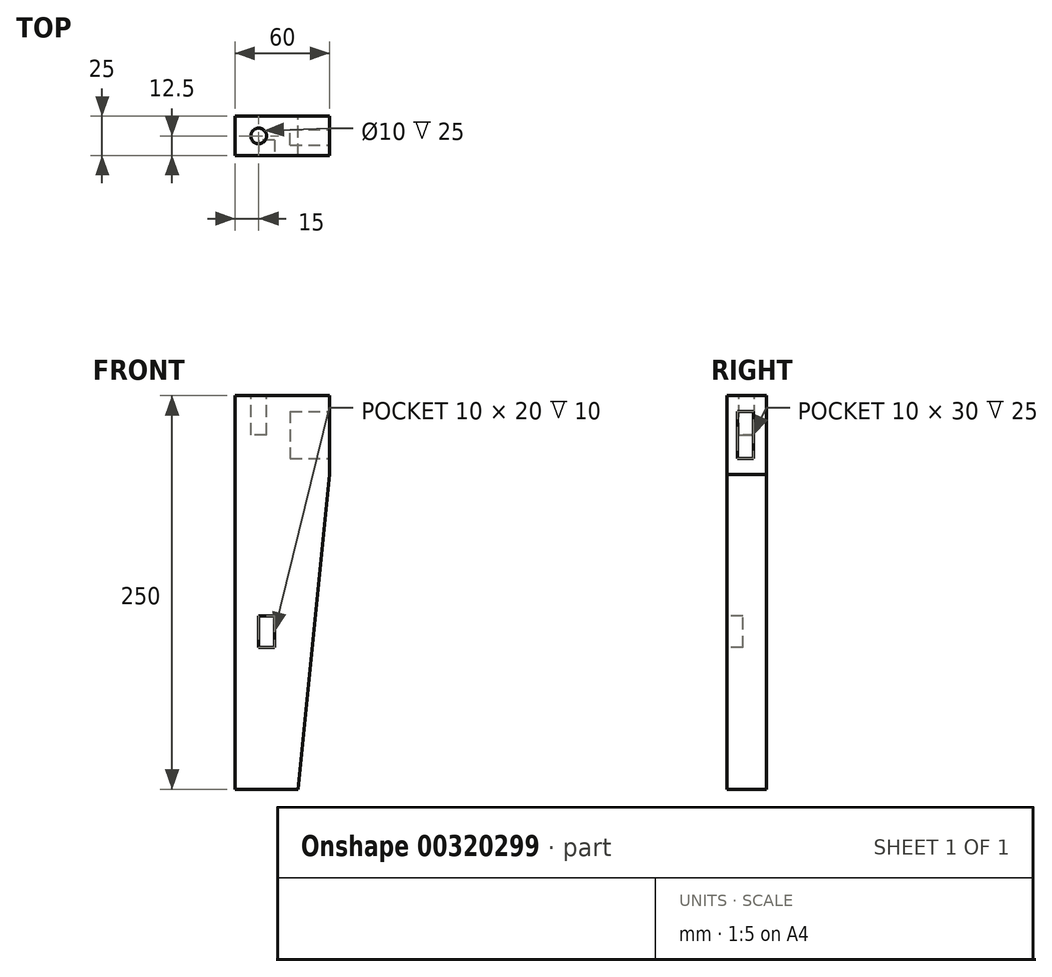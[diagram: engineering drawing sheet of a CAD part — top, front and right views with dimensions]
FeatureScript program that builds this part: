
annotation { "Feature Type Name" : "Feature", "Feature Type Description" : "" }
export const myFeature = defineFeature(function(context is Context, id is Id, definition is map)
    precondition{}
    {
        {
            var Q0;
            Q0=qCreatedBy(makeId("Front.planeOp"),FACE);
            var sketch = newSketch(context, id + "F0", { "sketchPlane" : qUnion([Q0])});
            skLineSegment(sketch, "E0.bottom", {"start": v(-30, 186.93) * mm, "end": v(30, 186.93) * mm});
            skLineSegment(sketch, "E0.left", {"start": v(-30, 186.93) * mm, "end": v(-30, -63.07) * mm});
            skPoint(sketch, "E0.middle", {"position": v(0, 61.93) * mm});
            skLineSegment(sketch, "E1", {"start": v(30, 186.93) * mm, "end": v(30, 136.93) * mm});
            skLineSegment(sketch, "E2", {"start": v(-30, -63.07) * mm, "end": v(10, -63.07) * mm});
            skLineSegment(sketch, "E3", {"start": v(30, 136.93) * mm, "end": v(10, -63.07) * mm});
            skSolve(sketch);
        }
        {
            var Q0;
            Q0=makeQuery(id+"F0.imprint","IMPRINT",FACE,{"disambiguationData":[TD([[makeQuery(id+"F0.imprint","IMPRINT",EDGE,{"derivedFrom":sQuery(id+"F0.wireOp",EDGE,"E0.bottom")}),-1.0]])]});
            var Q1;
            Q1 = qSketchRegion(id + "F2", true);
            extrude(context, id + "F1", {"entities" : qUnion([Q0, Q1]), "depth" : 25 * mm});
        }
        {
            var Q0;
            Q0=makeQuery(id+"F1.opExtrude","CAP_FACE",FACE,{"disambiguationData":[OSD([sQuery(id+"F0.wireOp",EDGE,"E0.bottom"),sQuery(id+"F0.wireOp",EDGE,"E0.left"),sQuery(id+"F0.wireOp",EDGE,"E1"),sQuery(id+"F0.wireOp",EDGE,"E2"),sQuery(id+"F0.wireOp",EDGE,"E3")])],"isStart":false});
            var sketch = newSketch(context, id + "F2", { "sketchPlane" : qUnion([Q0])});
            skLineSegment(sketch, "E4.bottom", {"start": v(-5, 26.93) * mm, "end": v(-15, 26.93) * mm});
            skLineSegment(sketch, "E4.top", {"start": v(-5, 46.93) * mm, "end": v(-15, 46.93) * mm});
            skLineSegment(sketch, "E4.left", {"start": v(-5, 26.93) * mm, "end": v(-5, 46.93) * mm});
            skLineSegment(sketch, "E4.right", {"start": v(-15, 26.93) * mm, "end": v(-15, 46.93) * mm});
            skPoint(sketch, "E4.middle", {"position": v(-10, 36.93) * mm});
            skSolve(sketch);
        }
        {
            var Q0;
            Q0=makeQuery(id+"F2.imprint","IMPRINT",FACE,{"disambiguationData":[TD([[makeQuery(id+"F2.imprint","IMPRINT",EDGE,{"derivedFrom":sQuery(id+"F2.wireOp",EDGE,"E4.bottom")}),-1.0]])]});
            extrude(context, id + "F3", {"entities" : qUnion([Q0]), "operationType" : NewBodyOperationType.REMOVE, "oppositeDirection" : true, "depth" : 10 * mm});
        }
        {
            var Q0;
            Q0=makeQuery(id+"F1.opExtrude","SWEPT_FACE",FACE,{"disambiguationData":[OSD([sQuery(id+"F0.wireOp",EDGE,"E1")])]});
            var sketch = newSketch(context, id + "F4", { "sketchPlane" : qUnion([Q0])});
            skLineSegment(sketch, "E5.bottom", {"start": v(-18.33, 176.93) * mm, "end": v(-8.33, 176.93) * mm});
            skLineSegment(sketch, "E5.top", {"start": v(-18.33, 146.93) * mm, "end": v(-8.33, 146.93) * mm});
            skLineSegment(sketch, "E5.left", {"start": v(-18.33, 176.93) * mm, "end": v(-18.33, 146.93) * mm});
            skLineSegment(sketch, "E5.right", {"start": v(-8.33, 176.93) * mm, "end": v(-8.33, 146.93) * mm});
            skSolve(sketch);
        }
        {
            var Q0;
            Q0=makeQuery(id+"F4.imprint","IMPRINT",FACE,{"disambiguationData":[TD([[makeQuery(id+"F4.imprint","IMPRINT",EDGE,{"derivedFrom":sQuery(id+"F4.wireOp",EDGE,"E5.bottom")}),-1.0]])]});
            extrude(context, id + "F5", {"entities" : qUnion([Q0]), "operationType" : NewBodyOperationType.REMOVE, "oppositeDirection" : true, "depth" : 25 * mm});
        }
        {
            var Q0;
            Q0=makeQuery(id+"F1.opExtrude","SWEPT_FACE",FACE,{"disambiguationData":[OSD([sQuery(id+"F0.wireOp",EDGE,"E0.bottom")])]});
            var sketch = newSketch(context, id + "F6", { "sketchPlane" : qUnion([Q0])});
            skCircle(sketch, "E6", {"center": v(-15, -12.5) * mm, "radius": 5 * mm});
            skSolve(sketch);
        }
        {
            var Q0;
            Q0=makeQuery(id+"F6.imprint","IMPRINT",FACE,{"disambiguationData":[TD([[makeQuery(id+"F6.imprint","IMPRINT",EDGE,{"derivedFrom":sQuery(id+"F6.wireOp",EDGE,"E6")}),1.0]])]});
            extrude(context, id + "F7", {"entities" : qUnion([Q0]), "operationType" : NewBodyOperationType.REMOVE, "oppositeDirection" : true, "depth" : 25 * mm});
        }
    });
